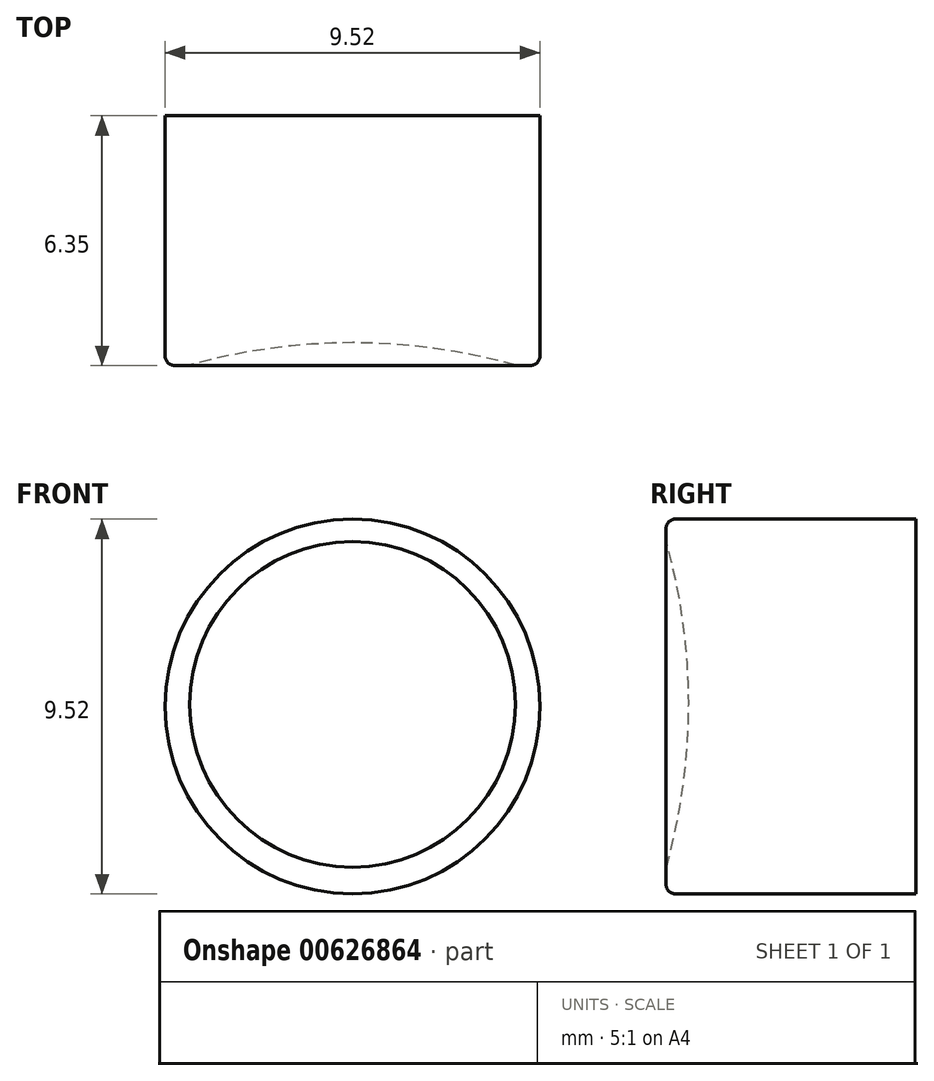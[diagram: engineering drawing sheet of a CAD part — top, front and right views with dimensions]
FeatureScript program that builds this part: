
annotation { "Feature Type Name" : "Feature", "Feature Type Description" : "" }
export const myFeature = defineFeature(function(context is Context, id is Id, definition is map)
    precondition{}
    {
        {
            var Q0;
            Q0=qCreatedBy(makeId("Front.planeOp"),FACE);
            var sketch = newSketch(context, id + "F0", { "sketchPlane" : qUnion([Q0])});
            skCircle(sketch, "E0", {"center": v(0, 0) * mm, "radius": 4.76 * mm});
            skSolve(sketch);
        }
        {
            var Q0;
            Q0 = qSketchRegion(id + "F0", true);
            extrude(context, id + "F1", {"entities" : qUnion([Q0]), "depth" : 6.35 * mm, "offsetDistance" : 25.4 * mm});
        }
        {
            var Q0;
            Q0=qCreatedBy(makeId("Right.planeOp"),FACE);
            var sketch = newSketch(context, id + "F2", { "sketchPlane" : qUnion([Q0])});
            skPoint(sketch, "E1.first.point", {"position": v(-6.35, 4.23) * mm});
            skPoint(sketch, "E1.second.point", {"position": v(-6.35, -4.12) * mm});
            skPoint(sketch, "E1.third.point", {"position": v(-36.06, 2.75) * mm});
            skLineSegment(sketch, "E2", {"start": v(-21.04, 15.32) * mm, "end": v(-21.04, -15.22) * mm, "construction": true});
            skLineSegment(sketch, "E3", {"start": v(-12.42, 12.66) * mm, "end": v(-12.42, -12.55) * mm});
            skArc(sketch, "E4.trimOffspring", {"start": v(-12.42, -12.55) * mm, "mid": v(-5.77, 0.05) * mm, "end": v(-12.42, 12.66) * mm});
            skSolve(sketch);
        }
        {
            var Q0;
            Q0 = qSketchRegion(id + "F2", true);
            var Q1;
            Q1=sQuery(id+"F2.wireOp",EDGE,"E2");
            revolve(context, id + "F3", {"operationType" : NewBodyOperationType.REMOVE, "entities" : qUnion([Q0]), "axis" : qUnion([Q1]), "revolveType" : RevolveType.FULL, "oppositeDirection" : true});
        }
        {
            var Q0;
            Q0=makeQuery(id+"F1.opExtrude","CAP_EDGE",EDGE,{"disambiguationData":[OSD([sQuery(id+"F0.wireOp",EDGE,"E0")])],"isStart":false});
            var Q1;
            Q1=makeQuery(id+"F3.boolean.opBoolean","INTERSECT",EDGE,{"derivedFrom":[makeQuery(id+"F1.opExtrude","CAP_FACE",FACE,{"disambiguationData":[OSD([sQuery(id+"F0.wireOp",EDGE,"E0")])],"isStart":false}),makeQuery(id+"F3.opRevolve","SWEPT_FACE",FACE,{"disambiguationData":[OSD([sQuery(id+"F2.wireOp",EDGE,"E4.trimOffspring")])]})]});
            fillet(context, id + "F4", {"entities" : qUnion([Q0, Q1]), "radius" : 0.25 * mm, "tangentPropagation" : true, "allowEdgeOverflow" : false});
        }
    });
